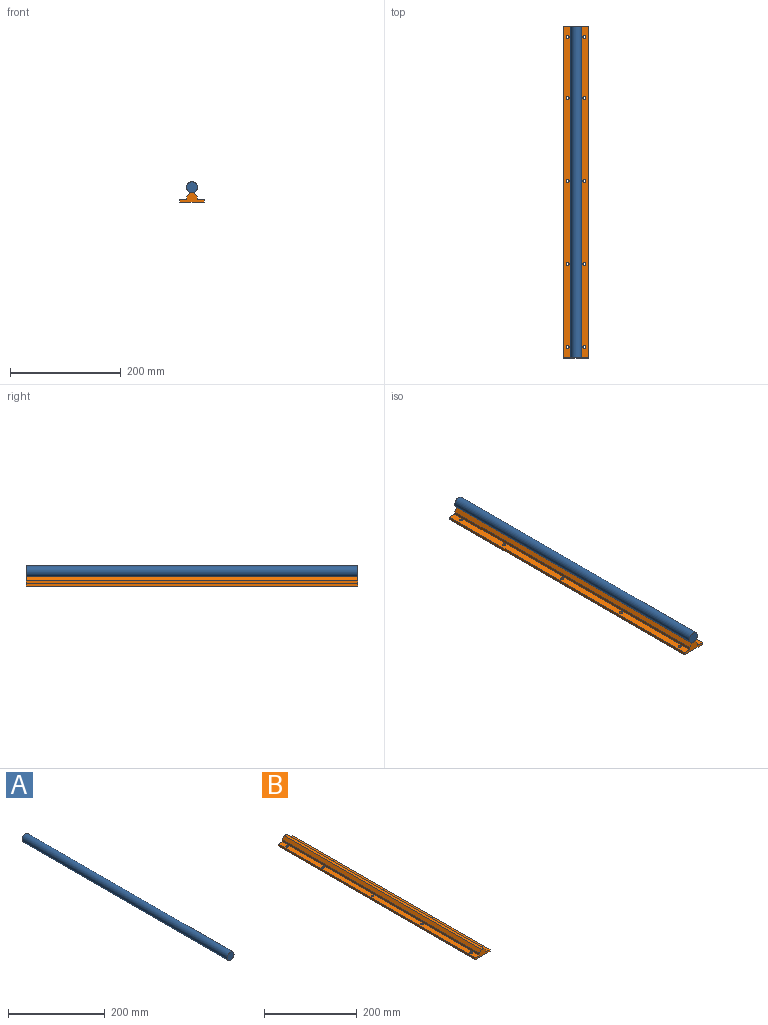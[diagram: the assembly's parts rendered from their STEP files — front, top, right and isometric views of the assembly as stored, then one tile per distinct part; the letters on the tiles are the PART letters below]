
ASSEMBLY  parts=2 mates=1
PART A: 3 faces, bbox 20x600x20 mm
  f0: cylinder r=10mm len=600mm, axis (0,-1,0), area 37699.1mm2, adj f1,f2
  f1: plane 20x20mm, normal (0,1,0), area 314.2mm2, adj f0
  f2: plane 20x20mm, normal (0,-1,0), area 314.2mm2, adj f0
PART B: 22 faces, bbox 45x600x17.8 mm
  f0: plane 600x45mm, normal (0,0,-1), area 26762.4mm2, adj f1,f9,f10,f11,f12,f13,f14,f15
  f1: plane 600x5mm, normal (1,0,0), area 3000mm2, adj f0,f2,f10,f11
  f2: plane 600x13mm, normal (0,0,1), area 7681.2mm2, adj f1,f3,f10,f11,f12,f15,f16,f19
  f3: plane 600x5mm, normal (1,0,0), area 3000mm2, adj f2,f4,f10,f11
  f4: plane 600x7.84mm, normal (0.82,0,0.57), area 5743.6mm2, adj f3,f5,f10,f11
  f5: cylinder r=10mm len=600mm, axis (0,-1,0), area 4938.2mm2, adj f4,f6,f10,f11
  f6: plane 600x7.84mm, normal (-0.82,0,0.57), area 5743.6mm2, adj f5,f7,f10,f11
  f7: plane 600x5mm, normal (-1,0,0), area 3000mm2, adj f6,f8,f10,f11
  f8: plane 600x13mm, normal (0,0,1), area 7681.2mm2, adj f7,f9,f10,f11,f13,f14,f17,f18
  f9: plane 600x5mm, normal (-1,0,0), area 3000mm2, adj f0,f8,f10,f11
  f10: plane 45x17.84mm, normal (0,1,0), area 421.3mm2, adj f0,f1,f2,f3,f4,f5,f6,f7
  f11: plane 45x17.84mm, normal (0,-1,0), area 421.3mm2, adj f0,f1,f2,f3,f4,f5,f6,f7
  f12: cylinder r=2.75mm len=5.5mm, axis (0,0,-1), area 86.4mm2, adj f0,f2
  f13: cylinder r=2.75mm len=5.5mm, axis (0,0,-1), area 86.4mm2, adj f0,f8
  f14: cylinder r=2.75mm len=5.5mm, axis (0,0,-1), area 86.4mm2, adj f0,f8
  f15: cylinder r=2.75mm len=5.5mm, axis (0,0,-1), area 86.4mm2, adj f0,f2
  f16: cylinder r=2.75mm len=5.5mm, axis (0,0,-1), area 86.4mm2, adj f0,f2
  f17: cylinder r=2.75mm len=5.5mm, axis (0,0,-1), area 86.4mm2, adj f0,f8
  f18: cylinder r=2.75mm len=5.5mm, axis (0,0,-1), area 86.4mm2, adj f0,f8
  f19: cylinder r=2.75mm len=5.5mm, axis (0,0,-1), area 86.4mm2, adj f0,f2
  f20: cylinder r=2.75mm len=5.5mm, axis (0,0,-1), area 86.4mm2, adj f0,f2
  f21: cylinder r=2.75mm len=5.5mm, axis (0,0,-1), area 86.4mm2, adj f0,f8
PLACE A at identity
PLACE B at identity
MATE fastened B.f11 <-> A.f2  axis (0,-1,0) through (22.5,0,0)mm
